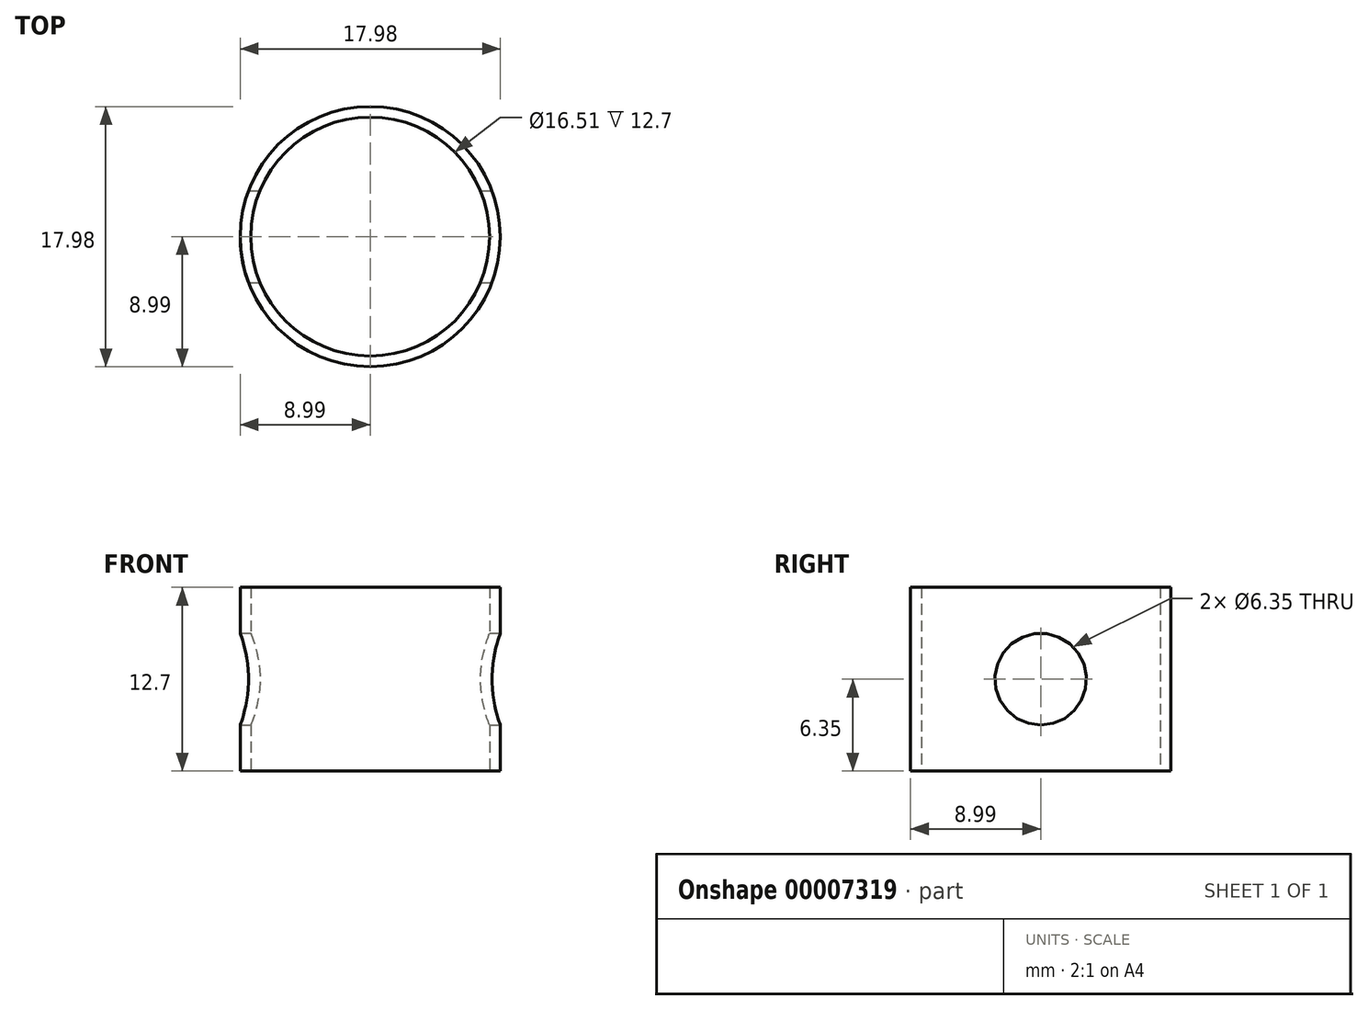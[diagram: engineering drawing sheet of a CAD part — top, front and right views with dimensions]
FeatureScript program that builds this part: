
annotation { "Feature Type Name" : "Feature", "Feature Type Description" : "" }
export const myFeature = defineFeature(function(context is Context, id is Id, definition is map)
    precondition{}
    {
        {
            var Q0;
            Q0=qCreatedBy(makeId("Front.planeOp"),FACE);
            var sketch = newSketch(context, id + "F0", { "sketchPlane" : qUnion([Q0])});
            skLineSegment(sketch, "E0", {"start": v(0, 0) * mm, "end": v(0, 12.7) * mm});
            skLineSegment(sketch, "E1", {"start": v(0, 12.7) * mm, "end": v(8.26, 12.7) * mm});
            skLineSegment(sketch, "E2", {"start": v(8.26, 12.7) * mm, "end": v(8.26, 0) * mm});
            skLineSegment(sketch, "E3", {"start": v(8.26, 0) * mm, "end": v(0, 0) * mm});
            skLineSegment(sketch, "E4", {"start": v(8.26, 0) * mm, "end": v(9, 0) * mm});
            skLineSegment(sketch, "E5", {"start": v(9, 0) * mm, "end": v(9, 12.7) * mm});
            skLineSegment(sketch, "E6", {"start": v(9, 12.7) * mm, "end": v(8.26, 12.7) * mm});
            skSolve(sketch);
        }
        {
            var Q0;
            Q0=makeQuery(id+"F0.imprint","IMPRINT",FACE,{"disambiguationData":[TD([[makeQuery(id+"F0.imprint","IMPRINT",EDGE,{"derivedFrom":sQuery(id+"F0.wireOp",EDGE,"E2")}),1.0]])]});
            var Q1;
            Q1=sQuery(id+"F0.wireOp",EDGE,"E0");
            revolve(context, id + "F1", {"entities" : qUnion([Q0]), "axis" : qUnion([Q1]), "revolveType" : RevolveType.FULL});
        }
        {
            var Q0;
            Q0=qCreatedBy(makeId("Right.planeOp"),FACE);
            var sketch = newSketch(context, id + "F2", { "sketchPlane" : qUnion([Q0])});
            skLineSegment(sketch, "E7", {"start": v(0, 0) * mm, "end": v(0, 12.7) * mm, "construction": true});
            skCircle(sketch, "E8", {"center": v(0, 6.35) * mm, "radius": 3.18 * mm});
            skSolve(sketch);
        }
        {
            var Q0;
            Q0=makeQuery(id+"F2.imprint","IMPRINT",FACE,{"disambiguationData":[TD([[makeQuery(id+"F2.imprint","IMPRINT",EDGE,{"derivedFrom":sQuery(id+"F2.wireOp",EDGE,"E8")}),1.0]])]});
            extrude(context, id + "F3", {"entities" : qUnion([Q0]), "operationType" : NewBodyOperationType.REMOVE, "oppositeDirection" : true, "depth" : 50.8 * mm, "symmetric" : true});
        }
    });
